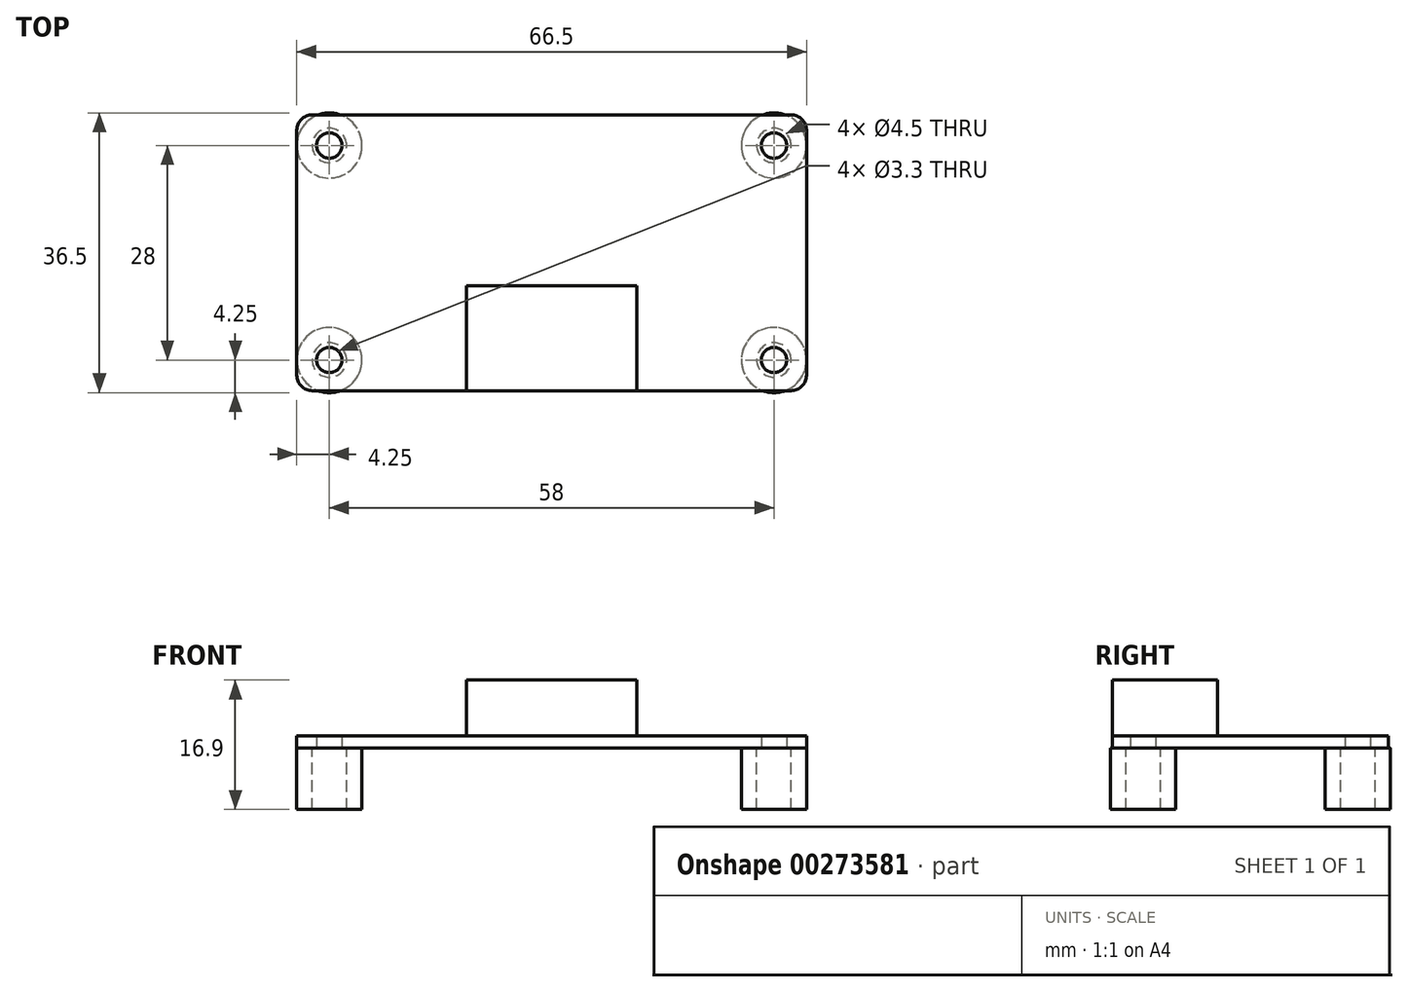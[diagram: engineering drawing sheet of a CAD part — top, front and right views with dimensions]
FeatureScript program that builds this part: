
annotation { "Feature Type Name" : "Feature", "Feature Type Description" : "" }
export const myFeature = defineFeature(function(context is Context, id is Id, definition is map)
    precondition{}
    {
        {
            var Q0;
            Q0=qCreatedBy(makeId("Top.planeOp"),FACE);
            var sketch = newSketch(context, id + "F0", { "sketchPlane" : qUnion([Q0])});
            skLineSegment(sketch, "E0.bottom", {"start": v(0, 0) * mm, "end": v(66.5, 0) * mm});
            skLineSegment(sketch, "E0.top", {"start": v(0, 36) * mm, "end": v(66.5, 36) * mm});
            skLineSegment(sketch, "E0.left", {"start": v(0, 0) * mm, "end": v(0, 36) * mm});
            skLineSegment(sketch, "E0.right", {"start": v(66.5, 0) * mm, "end": v(66.5, 36) * mm});
            skLineSegment(sketch, "E1", {"start": v(66.5, 36) * mm, "end": v(0, 0) * mm, "construction": true});
            skLineSegment(sketch, "E2.bottom", {"start": v(4.25, 32) * mm, "end": v(62.25, 32) * mm, "construction": true});
            skLineSegment(sketch, "E2.top", {"start": v(4.25, 4) * mm, "end": v(62.25, 4) * mm, "construction": true});
            skLineSegment(sketch, "E2.left", {"start": v(4.25, 32) * mm, "end": v(4.25, 4) * mm, "construction": true});
            skLineSegment(sketch, "E2.right", {"start": v(62.25, 32) * mm, "end": v(62.25, 4) * mm, "construction": true});
            skLineSegment(sketch, "E3", {"start": v(4.25, 32) * mm, "end": v(62.25, 4) * mm, "construction": true});
            skPoint(sketch, "E4", {"position": v(33.25, 18) * mm});
            skCircle(sketch, "E5", {"center": v(4.25, 32) * mm, "radius": 1.65 * mm});
            skCircle(sketch, "E6", {"center": v(62.25, 32) * mm, "radius": 1.65 * mm});
            skCircle(sketch, "E7", {"center": v(62.25, 4) * mm, "radius": 1.65 * mm});
            skCircle(sketch, "E8", {"center": v(4.25, 4) * mm, "radius": 1.65 * mm});
            skSolve(sketch);
        }
        {
            var Q0;
            Q0 = qSketchRegion(id + "F0", true);
            extrude(context, id + "F1", {"entities" : qUnion([Q0]), "depth" : 1.6 * mm});
        }
        {
            var Q0;
            Q0=makeQuery(id+"F1.opExtrude","SWEPT_EDGE",EDGE,{"disambiguationData":[OSD([sQuery(id+"F0.wireOp",EDGE,"E0.bottom"),sQuery(id+"F0.wireOp",EDGE,"E0.right")])]});
            var Q1;
            Q1=makeQuery(id+"F1.opExtrude","SWEPT_EDGE",EDGE,{"disambiguationData":[OSD([sQuery(id+"F0.wireOp",EDGE,"E0.bottom"),sQuery(id+"F0.wireOp",EDGE,"E0.left")])]});
            var Q2;
            Q2=makeQuery(id+"F1.opExtrude","SWEPT_EDGE",EDGE,{"disambiguationData":[OSD([sQuery(id+"F0.wireOp",EDGE,"E0.top"),sQuery(id+"F0.wireOp",EDGE,"E0.left")])]});
            var Q3;
            Q3=makeQuery(id+"F1.opExtrude","SWEPT_EDGE",EDGE,{"disambiguationData":[OSD([sQuery(id+"F0.wireOp",EDGE,"E0.top"),sQuery(id+"F0.wireOp",EDGE,"E0.right")])]});
            fillet(context, id + "F2", {"entities" : qUnion([Q0, Q1, Q2, Q3]), "radius" : 2 * mm, "tangentPropagation" : true, "allowEdgeOverflow" : false});
        }
        {
            var Q0;
            Q0=makeQuery(id+"F1.opExtrude","CAP_FACE",FACE,{"disambiguationData":[OSD([sQuery(id+"F0.wireOp",EDGE,"E0.bottom"),sQuery(id+"F0.wireOp",EDGE,"E0.top"),sQuery(id+"F0.wireOp",EDGE,"E0.left"),sQuery(id+"F0.wireOp",EDGE,"E0.right"),sQuery(id+"F0.wireOp",EDGE,"E5"),sQuery(id+"F0.wireOp",EDGE,"E6"),sQuery(id+"F0.wireOp",EDGE,"E7"),sQuery(id+"F0.wireOp",EDGE,"E8")])],"isStart":false});
            var sketch = newSketch(context, id + "F3", { "sketchPlane" : qUnion([Q0])});
            skLineSegment(sketch, "E9.bottom", {"start": v(22.15, 13.7) * mm, "end": v(44.35, 13.7) * mm});
            skLineSegment(sketch, "E9.top", {"start": v(22.15, 0) * mm, "end": v(44.35, 0) * mm});
            skLineSegment(sketch, "E9.left", {"start": v(22.15, 13.7) * mm, "end": v(22.15, 0) * mm});
            skLineSegment(sketch, "E9.right", {"start": v(44.35, 13.7) * mm, "end": v(44.35, 0) * mm});
            skPoint(sketch, "E10", {"position": v(33.25, 0) * mm});
            skSolve(sketch);
        }
        {
            var Q0;
            Q0 = qSketchRegion(id + "F3", true);
            extrude(context, id + "F4", {"entities" : qUnion([Q0]), "depth" : 7.3 * mm});
        }
        {
            var Q0;
            Q0=makeQuery(id+"F1.opExtrude","CAP_FACE",FACE,{"disambiguationData":[OSD([sQuery(id+"F0.wireOp",EDGE,"E0.bottom"),sQuery(id+"F0.wireOp",EDGE,"E0.top"),sQuery(id+"F0.wireOp",EDGE,"E0.left"),sQuery(id+"F0.wireOp",EDGE,"E0.right"),sQuery(id+"F0.wireOp",EDGE,"E5"),sQuery(id+"F0.wireOp",EDGE,"E6"),sQuery(id+"F0.wireOp",EDGE,"E7"),sQuery(id+"F0.wireOp",EDGE,"E8")])],"isStart":true});
            var sketch = newSketch(context, id + "F5", { "sketchPlane" : qUnion([Q0])});
            skCircle(sketch, "E11", {"center": v(4.25, -4) * mm, "radius": 2.25 * mm});
            skCircle(sketch, "E12", {"center": v(62.25, -4) * mm, "radius": 2.25 * mm});
            skCircle(sketch, "E13", {"center": v(62.25, -32) * mm, "radius": 2.25 * mm});
            skCircle(sketch, "E14", {"center": v(4.25, -32) * mm, "radius": 2.25 * mm});
            skCircle(sketch, "E15.0", {"center": v(4.25, -4) * mm, "radius": 4.25 * mm});
            skCircle(sketch, "E16.0", {"center": v(62.25, -4) * mm, "radius": 4.25 * mm});
            skCircle(sketch, "E17.0", {"center": v(4.25, -32) * mm, "radius": 4.25 * mm});
            skCircle(sketch, "E18.0", {"center": v(62.25, -32) * mm, "radius": 4.25 * mm});
            skSolve(sketch);
        }
        {
            var Q0;
            Q0 = qSketchRegion(id + "F5", true);
            extrude(context, id + "F6", {"entities" : qUnion([Q0]), "depth" : 8 * mm});
        }
    });
